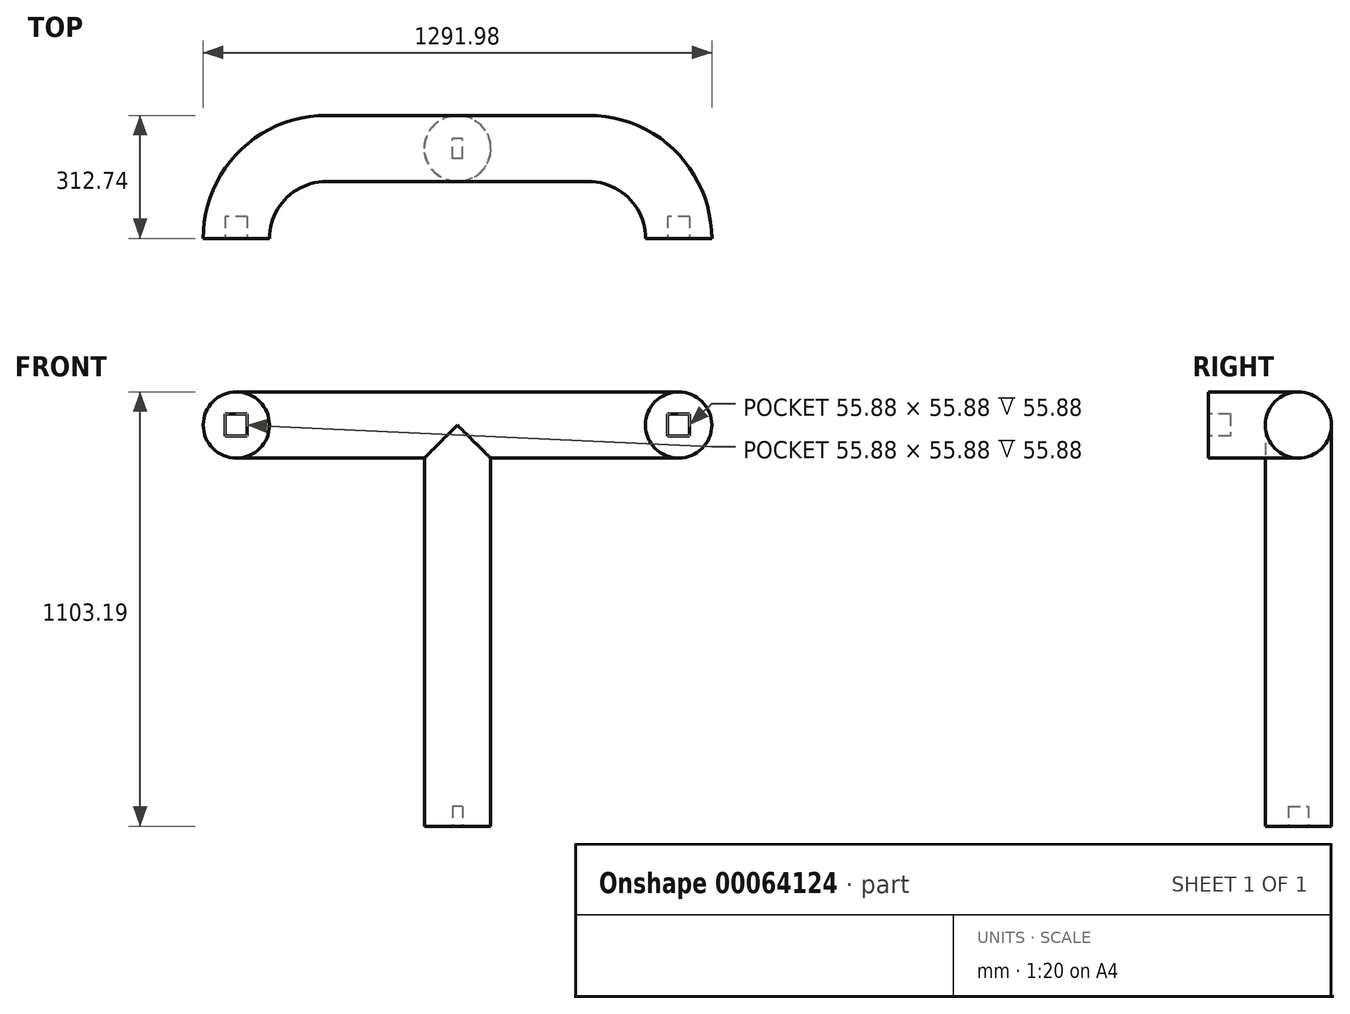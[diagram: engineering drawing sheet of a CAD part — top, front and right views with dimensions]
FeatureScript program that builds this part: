
annotation { "Feature Type Name" : "Feature", "Feature Type Description" : "" }
export const myFeature = defineFeature(function(context is Context, id is Id, definition is map)
    precondition{}
    {
        {
            var Q0;
            Q0=qCreatedBy(makeId("Top.planeOp"),FACE);
            var sketch = newSketch(context, id + "F0", { "sketchPlane" : qUnion([Q0])});
            skCircle(sketch, "E0", {"center": v(0, 0) * mm, "radius": 84.14 * mm});
            skSolve(sketch);
        }
        {
            var Q0;
            Q0=qCreatedBy(makeId("Top.planeOp"),FACE);
            cPlane(context, id + "F1", {"entities" : qUnion([Q0]), "cplaneType" : CPlaneType.OFFSET, "offset" : 1019.05 * mm, "width" : 152.4 * mm, "height" : 152.4 * mm});
        }
        {
            var Q0;
            Q0=makeQuery(id+"F0.imprint","IMPRINT",FACE,{"disambiguationData":[TD([[makeQuery(id+"F0.imprint","IMPRINT",EDGE,{"derivedFrom":sQuery(id+"F0.wireOp",EDGE,"E0")}),1.0]])]});
            extrude(context, id + "F2", {"entities" : qUnion([Q0]), "depth" : 1019.05 * mm, "offsetDistance" : 25.4 * mm});
        }
        {
            var Q0;
            Q0=qCreatedBy(id+"F1.planeOp",FACE);
            var sketch = newSketch(context, id + "F3", { "sketchPlane" : qUnion([Q0])});
            skLineSegment(sketch, "E1", {"start": v(0, 0) * mm, "end": v(-333.25, 0) * mm});
            skLineSegment(sketch, "E2", {"start": v(-333.25, 0) * mm, "end": v(-333.25, -228.6) * mm, "construction": true});
            skArc(sketch, "E3", {"start": v(-333.25, 0) * mm, "mid": v(-494.9, -66.96) * mm, "end": v(-561.85, -228.6) * mm});
            skLineSegment(sketch, "E4", {"start": v(-333.25, -228.6) * mm, "end": v(-561.85, -228.6) * mm, "construction": true});
            skLineSegment(sketch, "E5", {"start": v(0, 0) * mm, "end": v(0, -190.78) * mm, "construction": true});
            skLineSegment(sketch, "E6.MirrorCS", {"start": v(333.25, -228.6) * mm, "end": v(561.85, -228.6) * mm, "construction": true});
            skLineSegment(sketch, "E7.MirrorCS", {"start": v(0, 0) * mm, "end": v(333.25, 0) * mm});
            skArc(sketch, "E8.MirrorCS", {"start": v(333.25, 0) * mm, "mid": v(494.9, -66.96) * mm, "end": v(561.85, -228.6) * mm});
            skLineSegment(sketch, "E9.MirrorCS", {"start": v(333.25, 0) * mm, "end": v(333.25, -228.6) * mm, "construction": true});
            skSolve(sketch);
        }
        {
            var Q0;
            Q0=qCreatedBy(makeId("Right.planeOp"),FACE);
            var sketch = newSketch(context, id + "F4", { "sketchPlane" : qUnion([Q0])});
            skLineSegment(sketch, "E10", {"start": v(0, 0) * mm, "end": v(0, 1019.05) * mm, "construction": true});
            skCircle(sketch, "E11", {"center": v(0, 1019.05) * mm, "radius": 84.14 * mm});
            skSolve(sketch);
        }
        {
            var Q0;
            Q0=makeQuery(id+"F4.imprint","IMPRINT",FACE,{"disambiguationData":[TD([[makeQuery(id+"F4.imprint","IMPRINT",EDGE,{"derivedFrom":sQuery(id+"F4.wireOp",EDGE,"E11")}),1.0]])]});
            var Q1;
            Q1=sQuery(id+"F4.wireOp",EDGE,"E11");
            var Q2;
            Q2=sQuery(id+"F3.wireOp",EDGE,"E1");
            var Q3;
            Q3=sQuery(id+"F3.wireOp",EDGE,"E3");
            sweep(context, id + "F5", {"operationType" : NewBodyOperationType.ADD, "profiles" : qUnion([Q0]), "surfaceProfiles" : qUnion([Q1]), "path" : qUnion([Q2, Q3])});
        }
        {
            var Q0;
            Q0=makeQuery(id+"F4.imprint","IMPRINT",FACE,{"disambiguationData":[TD([[makeQuery(id+"F4.imprint","IMPRINT",EDGE,{"derivedFrom":sQuery(id+"F4.wireOp",EDGE,"E11")}),1.0]])]});
            var Q1;
            Q1=sQuery(id+"F3.wireOp",EDGE,"E7.MirrorCS");
            var Q2;
            Q2=sQuery(id+"F3.wireOp",EDGE,"E8.MirrorCS");
            sweep(context, id + "F6", {"operationType" : NewBodyOperationType.ADD, "profiles" : qUnion([Q0]), "path" : qUnion([Q1, Q2])});
        }
        {
            var Q0;
            Q0=makeQuery(id+"F5.opSweep","CAP_FACE",FACE,{"disambiguationData":[OSD([sQuery(id+"F3.wireOp",VERTEX,"E3.end"),sQuery(id+"F4.wireOp",EDGE,"E11")])],"isStart":false});
            var sketch = newSketch(context, id + "F7", { "sketchPlane" : qUnion([Q0])});
            skLineSegment(sketch, "E12.bottom", {"start": v(-533.9, 1046.99) * mm, "end": v(-589.79, 1046.99) * mm});
            skLineSegment(sketch, "E12.top", {"start": v(-533.9, 991.1) * mm, "end": v(-589.79, 991.1) * mm});
            skLineSegment(sketch, "E12.left", {"start": v(-533.9, 1046.99) * mm, "end": v(-533.9, 991.1) * mm});
            skLineSegment(sketch, "E12.right", {"start": v(-589.79, 1046.99) * mm, "end": v(-589.79, 991.1) * mm});
            skPoint(sketch, "E12.middle", {"position": v(-561.85, 1019.05) * mm});
            skSolve(sketch);
        }
        {
            var Q0;
            Q0=makeQuery(id+"F6.opSweep","CAP_FACE",FACE,{"disambiguationData":[OSD([sQuery(id+"F3.wireOp",VERTEX,"E8.MirrorCS.end"),sQuery(id+"F4.wireOp",EDGE,"E11")])],"isStart":false});
            var sketch = newSketch(context, id + "F8", { "sketchPlane" : qUnion([Q0])});
            skLineSegment(sketch, "E13.bottom", {"start": v(589.79, 1046.99) * mm, "end": v(533.9, 1046.99) * mm});
            skLineSegment(sketch, "E13.top", {"start": v(589.79, 991.1) * mm, "end": v(533.9, 991.1) * mm});
            skLineSegment(sketch, "E13.left", {"start": v(589.79, 1046.99) * mm, "end": v(589.79, 991.1) * mm});
            skLineSegment(sketch, "E13.right", {"start": v(533.9, 1046.99) * mm, "end": v(533.9, 991.1) * mm});
            skPoint(sketch, "E13.middle", {"position": v(561.85, 1019.05) * mm});
            skSolve(sketch);
        }
        {
            var Q0;
            Q0=makeQuery(id+"F7.imprint","IMPRINT",FACE,{"disambiguationData":[TD([[makeQuery(id+"F7.imprint","IMPRINT",EDGE,{"derivedFrom":sQuery(id+"F7.wireOp",EDGE,"E12.bottom")}),1.0]])]});
            var Q1;
            Q1=makeQuery(id+"F8.imprint","IMPRINT",FACE,{"disambiguationData":[TD([[makeQuery(id+"F8.imprint","IMPRINT",EDGE,{"derivedFrom":sQuery(id+"F8.wireOp",EDGE,"E13.bottom")}),1.0]])]});
            extrude(context, id + "F9", {"entities" : qUnion([Q0, Q1]), "operationType" : NewBodyOperationType.REMOVE, "oppositeDirection" : true, "depth" : 55.88 * mm, "offsetDistance" : 25.4 * mm});
        }
        {
            var Q0;
            Q0=makeQuery(id+"F2.opExtrude","CAP_FACE",FACE,{"disambiguationData":[OSD([sQuery(id+"F0.wireOp",EDGE,"E0")])],"isStart":true});
            var sketch = newSketch(context, id + "F10", { "sketchPlane" : qUnion([Q0])});
            skLineSegment(sketch, "E14.bottom", {"start": v(12.7, 25.4) * mm, "end": v(-12.7, 25.4) * mm});
            skLineSegment(sketch, "E14.top", {"start": v(12.7, -25.4) * mm, "end": v(-12.7, -25.4) * mm});
            skLineSegment(sketch, "E14.left", {"start": v(12.7, 25.4) * mm, "end": v(12.7, -25.4) * mm});
            skLineSegment(sketch, "E14.right", {"start": v(-12.7, 25.4) * mm, "end": v(-12.7, -25.4) * mm});
            skPoint(sketch, "E14.middle", {"position": v(0, 0) * mm});
            skSolve(sketch);
        }
        {
            var Q0;
            Q0=makeQuery(id+"F10.imprint","IMPRINT",FACE,{"disambiguationData":[TD([[makeQuery(id+"F10.imprint","IMPRINT",EDGE,{"derivedFrom":sQuery(id+"F10.wireOp",EDGE,"E14.bottom")}),1.0]])]});
            extrude(context, id + "F11", {"entities" : qUnion([Q0]), "operationType" : NewBodyOperationType.REMOVE, "oppositeDirection" : true, "depth" : 50.8 * mm, "offsetDistance" : 25.4 * mm});
        }
    });
